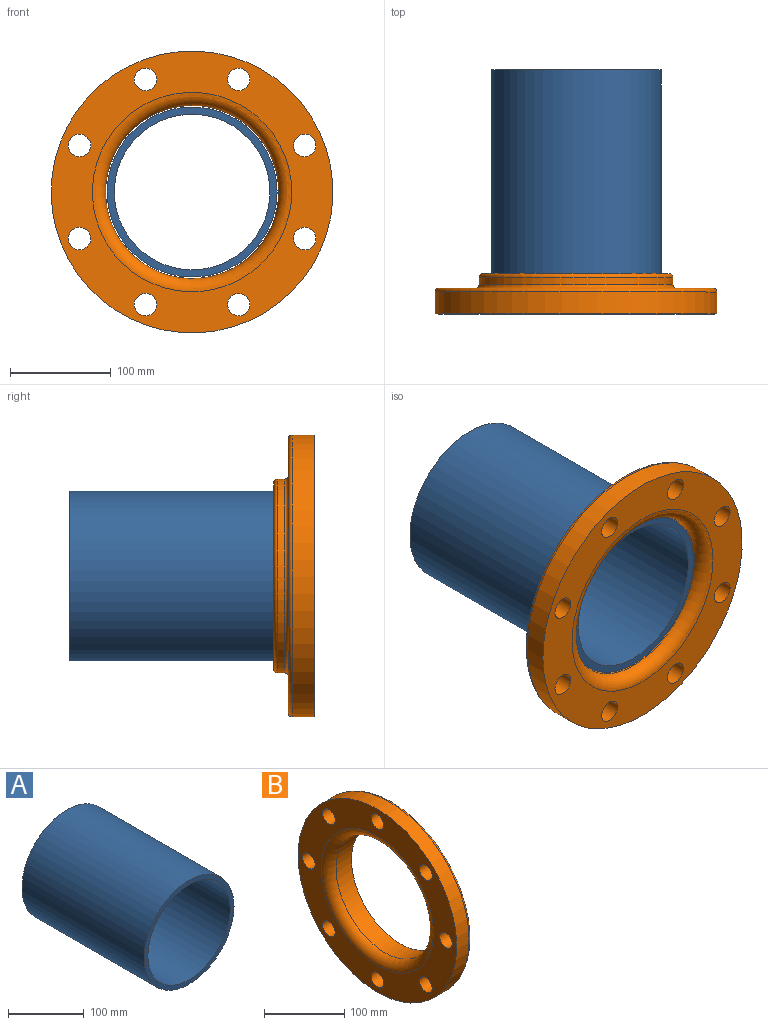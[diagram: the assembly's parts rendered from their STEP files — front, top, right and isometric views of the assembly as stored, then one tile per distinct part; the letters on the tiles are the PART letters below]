
ASSEMBLY  parts=2 mates=1
PART A: 4 faces, bbox 168.3x228.6x168.3 mm
  f0: plane 168.28x168.28mm, normal (0,-1,0), area 3600.9mm2, adj f2,f3
  f1: plane 168.28x168.28mm, normal (0,1,0), area 3600.9mm2, adj f2,f3
  f2: cylinder r=84.14mm len=228.6mm, axis (0,1,0), area 120849.7mm2, adj f0,f1
  f3: cylinder r=77.03mm len=228.6mm, axis (0,1,0), area 110634.5mm2, adj f0,f1
PART B: 18 faces, bbox 40x302x302 mm
  f0: cylinder r=85.7mm len=171.4mm, axis (1,0,0), area 14538.7mm2, adj f2,f17
  f1: plane 279x279mm, normal (-1,0,0), area 27435.2mm2, adj f8,f9,f10,f11,f12,f13,f14,f15
  f2: plane 184.5x184.5mm, normal (1,0,0), area 3661.8mm2, adj f0,f3
  f3: torus R=92.25mm, axis (-1,0,0), area 3502.5mm2, adj f2,f4
  f4: cylinder r=96mm len=192mm, axis (-1,0,0), area 4282.8mm2, adj f3,f5
  f5: torus R=99.75mm, axis (-1,0,0), area 3603.4mm2, adj f4,f6
  f6: plane 271.5x271.5mm, normal (1,0,0), area 23538mm2, adj f5,f7,f9,f10,f11,f12,f13,f14
  f7: torus R=135.75mm, axis (-1,0,0), area 5112.4mm2, adj f6,f8
  f8: cylinder r=139.5mm len=279mm, axis (-1,0,0), area 18976.4mm2, adj f1,f7
  f9: cylinder r=11.1mm len=25.4mm, axis (1,0,0), area 1771.5mm2, adj f1,f6
  f10: cylinder r=11.1mm len=25.4mm, axis (1,0,0), area 1771.5mm2, adj f1,f6
  f11: cylinder r=11.1mm len=25.4mm, axis (1,0,0), area 1771.5mm2, adj f1,f6
  f12: cylinder r=11.1mm len=25.4mm, axis (1,0,0), area 1771.5mm2, adj f1,f6
  f13: cylinder r=11.1mm len=25.4mm, axis (1,0,0), area 1771.5mm2, adj f1,f6
  f14: cylinder r=11.1mm len=25.4mm, axis (1,0,0), area 1771.5mm2, adj f1,f6
  f15: cylinder r=11.1mm len=25.4mm, axis (1,0,0), area 1771.5mm2, adj f1,f6
  f16: cylinder r=11.1mm len=25.4mm, axis (1,0,0), area 1771.5mm2, adj f1,f6
  f17: torus R=98.7mm, axis (-1,0,0), area 11601.8mm2, adj f0,f1
PLACE A t=(3298.47,908.69,0)mm fixed
PLACE B rot(axis=(0.19,0.19,0.96),92.2deg) t=(0,-12.7,0)mm
MATE fastened A.f2 <-> B.f17  axis (0,1,0) through (0,0.3,0)mm
